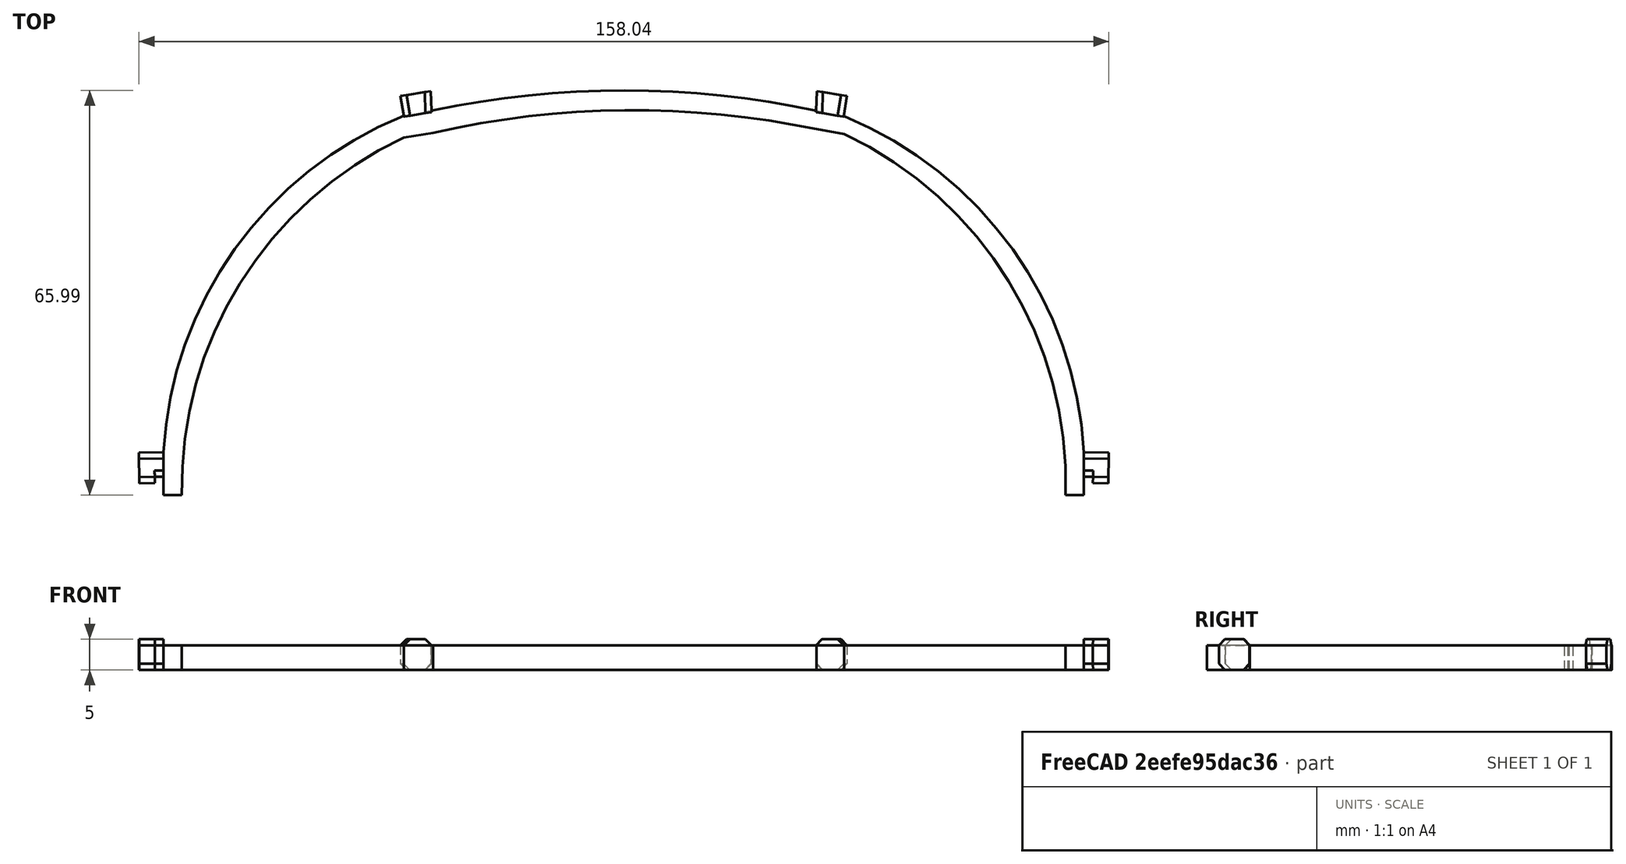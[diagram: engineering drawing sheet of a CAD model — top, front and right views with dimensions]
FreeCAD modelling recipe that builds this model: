
FCSTD DOCUMENT  (FreeCAD 0.18R4 (GitTag))
Label: arco_inferior
License: CreativeCommons Attribution-ShareAlike
LicenseURL: http://creativecommons.org/licenses/by-sa/4.0/
objects: Part::Cut×7, Part::Box×6, Part::Feature×1, Part::Cylinder×1, Sketcher::SketchObject×1, Part::Extrusion×1, Part::MultiFuse×1
note: 18 computed .brp shape members not serialized (recipe doc carries the construction recipe); baked Part::Feature solids carry a one-line shape summary decoded from their .brp

FEATURE [Part::Feature] ___________________v2iyk6001_solid001  label="v2iyk6001 (Solid)001"
  shape: bbox 158 x 181 x 5 mm, 2210 faces (baked)
FEATURE [Part::Cylinder] Cylinder
  Angle = 360
  AttacherType = Attacher::AttachEngine3D
  Height = 10
  Placement = pos=(0,-98,0) rot=(0,0,1;0rad)
  Radius = 98
FEATURE [Part::Cut] Cut
  Base = -> ___________________v2iyk6001_solid001
  Tool = -> Cylinder
FEATURE [Part::Box] Box  label="Cube"
  AttacherType = Attacher::AttachEngine3D
  Height = 10
  Length = 200
  Placement = pos=(-100,-27,0) rot=(0,0,1;0rad)
  Width = 52
FEATURE [Part::Cut] Cut001
  Base = -> Cut
  Tool = -> Box
FEATURE [Part::Box] Box001  label="Cube001"
  AttacherType = Attacher::AttachEngine3D
  Height = 10
  Length = 61
  Placement = pos=(-30,22,0) rot=(0,0,1;0rad)
  Width = 10
FEATURE [Part::Cut] Cut002
  Base = -> Cut001
  Tool = -> Box001
FEATURE [Part::Box] Box002  label="Cube002"
  AttacherType = Attacher::AttachEngine3D
  Height = 10
  Length = 16
  Placement = pos=(27,18,0) rot=(0,0,1;-0.15708rad)
  Width = 10
FEATURE [Part::Box] Box003  label="Cube003"
  AttacherType = Attacher::AttachEngine3D
  Height = 10
  Length = 16
  Placement = pos=(-27,18,7) rot=(-0.078459,0.996917,0;3.14159rad)
  Width = 10
FEATURE [Part::Cut] Cut003
  Base = -> Cut002
  Tool = -> Box002
FEATURE [Part::Cut] Cut004
  Base = -> Cut003
  Tool = -> Box003
FEATURE [Part::Box] Box004  label="Cube004"
  AttacherType = Attacher::AttachEngine3D
  Height = 10
  Length = 10
  Placement = pos=(65,-37,0) rot=(0,0,1;0rad)
  Width = 16
FEATURE [Part::Box] Box005  label="Cube005"
  AttacherType = Attacher::AttachEngine3D
  Height = 10
  Length = 10
  Placement = pos=(-75,-37,0) rot=(0,0,1;0rad)
  Width = 16
FEATURE [Part::Cut] Cut005
  Base = -> Cut004
  Tool = -> Box004
FEATURE [Part::Cut] Cut006
  Base = -> Cut005
  Tool = -> Box005
FEATURE [Sketcher::SketchObject] Sketch
  ExternalGeometry = -> [Cut006]
  sketch-geometry (14):
    g0: ArcOfCircle CenterX=-12.193 CenterY=-31.4186 CenterZ=0 NormalX=0 NormalY=0 NormalZ=1 AngleXU=0 Radius=62.9 StartAngle=1.95569 EndAngle=3.08722
    g1: ArcOfCircle CenterX=12.197 CenterY=-31.4975 CenterZ=0 NormalX=0 NormalY=0 NormalZ=1 AngleXU=0 Radius=62.9003 StartAngle=0.0556389 EndAngle=1.18457
    g2: ArcOfCircle CenterX=0.00302871 CenterY=-119.006 CenterZ=0 NormalX=0 NormalY=0 NormalZ=1 AngleXU=0 Radius=150 StartAngle=1.35993 EndAngle=1.77941
    g3: LineSegment StartX=-35.8096 StartY=26.8795 StartZ=0 EndX=-31.0621 EndY=27.7414 EndZ=0
    g4: LineSegment StartX=31.399 StartY=27.671 StartZ=0 EndX=35.891 EndY=26.7695 EndZ=0
    g5: LineSegment StartX=75 StartY=-27.9996 StartZ=0 EndX=75 EndY=-34.9996 EndZ=0
    g6: LineSegment StartX=-75 StartY=-28.0001 StartZ=0 EndX=-75 EndY=-35.0001 EndZ=0
    g7: LineSegment StartX=-75 StartY=-35.0001 StartZ=0 EndX=-72 EndY=-35.0001 EndZ=0
    g8: LineSegment StartX=75 StartY=-34.9996 StartZ=0 EndX=71.9901 EndY=-34.9789 EndZ=0
    g9: ArcOfCircle CenterX=-9.1143 CenterY=-33.659 CenterZ=0 NormalX=0 NormalY=0 NormalZ=1 AngleXU=0 Radius=62.9 StartAngle=2.0091 EndAngle=3.16292
    g10: ArcOfCircle CenterX=9.12048 CenterY=-33.0252 CenterZ=0 NormalX=0 NormalY=0 NormalZ=1 AngleXU=0 Radius=62.9 StartAngle=6.25212 EndAngle=7.41435
    g11: ArcOfCircle CenterX=1.52215 CenterY=-118.418 CenterZ=0 NormalX=0 NormalY=0 NormalZ=1 AngleXU=0 Radius=146.177 StartAngle=1.36479 EndAngle=1.79559
    g12: LineSegment StartX=-35.8096 StartY=23.2952 StartZ=0 EndX=-31.0621 EndY=24.0815 EndZ=0
    g13: LineSegment StartX=31.4226 StartY=24.6687 StartZ=0 EndX=35.891 EndY=23.8936 EndZ=0
  constraints (16):
    c: Coincident(g11,g12)
    c: Coincident(g9,g12)
    c: Coincident(g2,g3)
    c: Coincident(g0,g3)
    c: Coincident(g2,g4)
    c: Coincident(g11,g13)
    c: Coincident(g1,g4)
    c: Coincident(g10,g13)
    c: Coincident(g1,g5)
    c: Coincident(g1,g-4)
    c: Coincident(g5,g8)
    c: Coincident(g8,g10)
    c: Coincident(g0,g6)
    c: Coincident(g0,g-3)
    c: Coincident(g6,g7)
    c: Coincident(g7,g9)
FEATURE [Part::Extrusion] Extrude
  Base = -> Sketch
  Dir = (0,0,1)
  DirMode = 2
  FaceMakerClass = Part::FaceMakerBullseye
  LengthFwd = 4
  LengthRev = 0
  Solid = true
  Symmetric = false
FEATURE [Part::MultiFuse] Fusion
  Shapes = -> [Cut006,Extrude]
